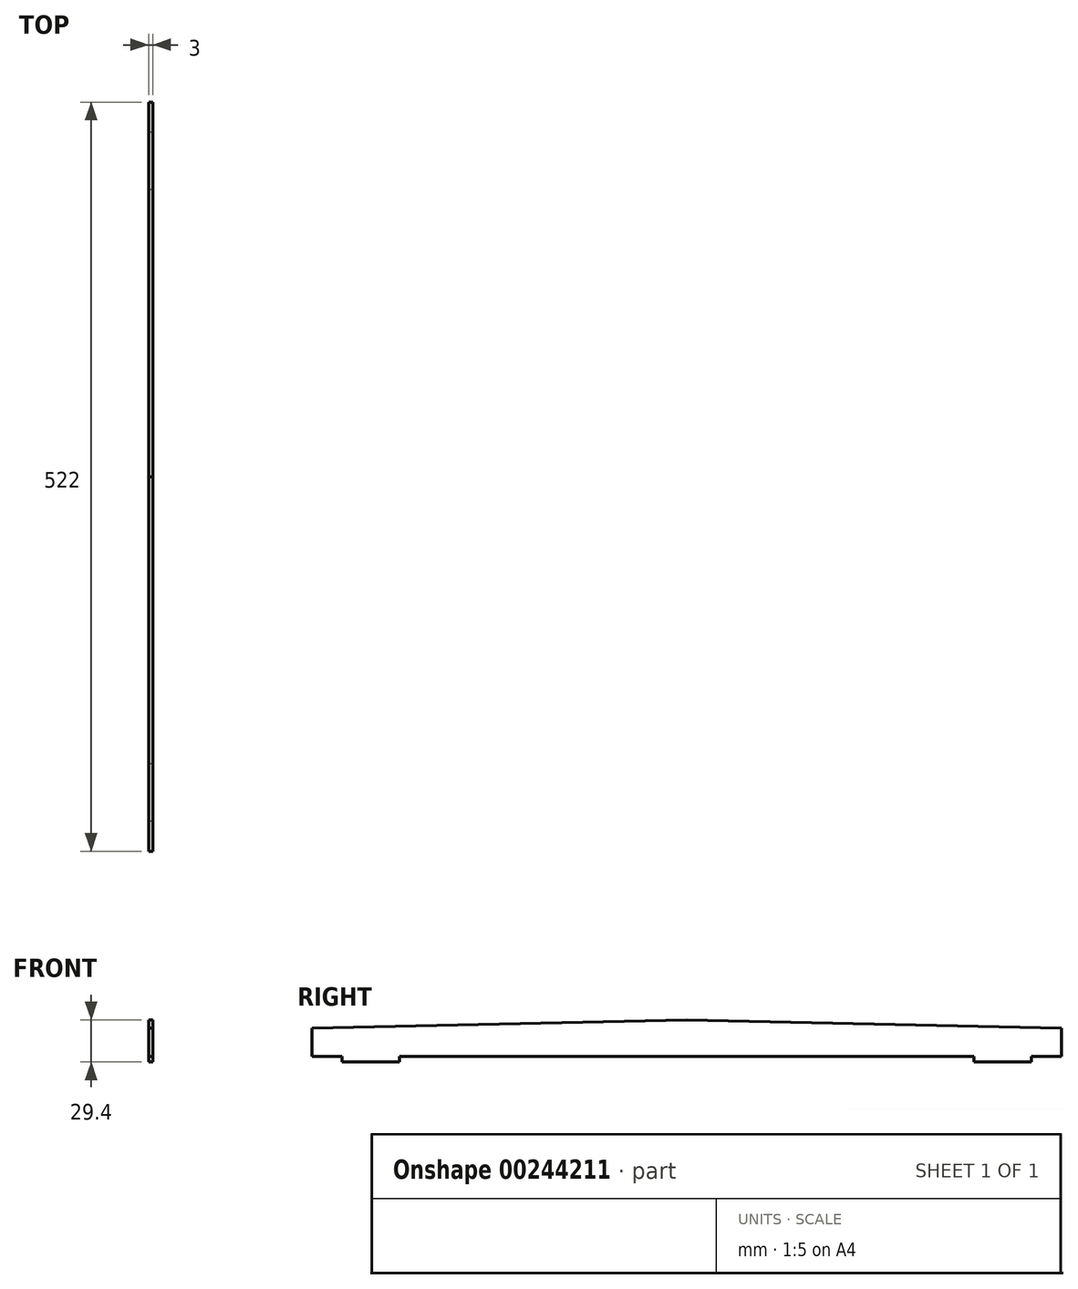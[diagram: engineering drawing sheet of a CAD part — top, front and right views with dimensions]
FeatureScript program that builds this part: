
annotation { "Feature Type Name" : "Feature", "Feature Type Description" : "" }
export const myFeature = defineFeature(function(context is Context, id is Id, definition is map)
    precondition{}
    {
        {
            var Q0;
            Q0=qCreatedBy(makeId("Right.planeOp"),FACE);
            var sketch = newSketch(context, id + "F0", { "sketchPlane" : qUnion([Q0])});
            skLineSegment(sketch, "E0", {"start": v(-14.7, 0) * mm, "end": v(-9.03, 261) * mm});
            skLineSegment(sketch, "E1", {"start": v(-9.03, 261) * mm, "end": v(10.7, 261) * mm});
            skLineSegment(sketch, "E2", {"start": v(10.7, 261) * mm, "end": v(10.7, 240) * mm});
            skLineSegment(sketch, "E3", {"start": v(10.7, 240) * mm, "end": v(14.7, 240) * mm});
            skLineSegment(sketch, "E4", {"start": v(14.7, 240) * mm, "end": v(14.7, 200) * mm});
            skLineSegment(sketch, "E5", {"start": v(14.7, 200) * mm, "end": v(10.7, 200) * mm});
            skLineSegment(sketch, "E6", {"start": v(10.7, 200) * mm, "end": v(10.7, -200) * mm});
            skLineSegment(sketch, "E7", {"start": v(10.7, -200) * mm, "end": v(14.7, -200) * mm});
            skLineSegment(sketch, "E8", {"start": v(14.7, -200) * mm, "end": v(14.7, -240) * mm});
            skLineSegment(sketch, "E9", {"start": v(14.7, -240) * mm, "end": v(10.7, -240) * mm});
            skLineSegment(sketch, "E10", {"start": v(10.7, -240) * mm, "end": v(10.7, -261) * mm});
            skLineSegment(sketch, "E11", {"start": v(10.7, -261) * mm, "end": v(-9.03, -261) * mm});
            skLineSegment(sketch, "E12", {"start": v(-9.03, -261) * mm, "end": v(-14.7, 0) * mm});
            skSolve(sketch);
        }
        {
            var Q0;
            Q0 = qSketchRegion(id + "F0", true);
            extrude(context, id + "F1", {"entities" : qUnion([Q0]), "depth" : 3 * mm});
        }
        {
            var Q0;
            Q0=makeQuery(id+"F1.opExtrude","SWEPT_BODY",BODY,{"disambiguationData":[OSD([sQuery(id+"F0.wireOp",EDGE,"E0"),sQuery(id+"F0.wireOp",EDGE,"E1"),sQuery(id+"F0.wireOp",EDGE,"E2"),sQuery(id+"F0.wireOp",EDGE,"E3"),sQuery(id+"F0.wireOp",EDGE,"E4"),sQuery(id+"F0.wireOp",EDGE,"E5"),sQuery(id+"F0.wireOp",EDGE,"E6"),sQuery(id+"F0.wireOp",EDGE,"E7"),sQuery(id+"F0.wireOp",EDGE,"E8"),sQuery(id+"F0.wireOp",EDGE,"E9"),sQuery(id+"F0.wireOp",EDGE,"E10"),sQuery(id+"F0.wireOp",EDGE,"E11"),sQuery(id+"F0.wireOp",EDGE,"E12")])]});
            var Q1;
            Q1=makeQuery(id+"F1.opExtrude","SWEPT_EDGE",EDGE,{"disambiguationData":[OSD([sQuery(id+"F0.wireOp",EDGE,"E7"),sQuery(id+"F0.wireOp",EDGE,"E8")])]});
            transform(context, id + "F2", {"entities" : qUnion([Q0]), "transformType" : TransformType.ROTATION, "transformAxis" : qUnion([Q1]), "angle" : 90 * degree, "makeCopy" : false});
        }
    });
